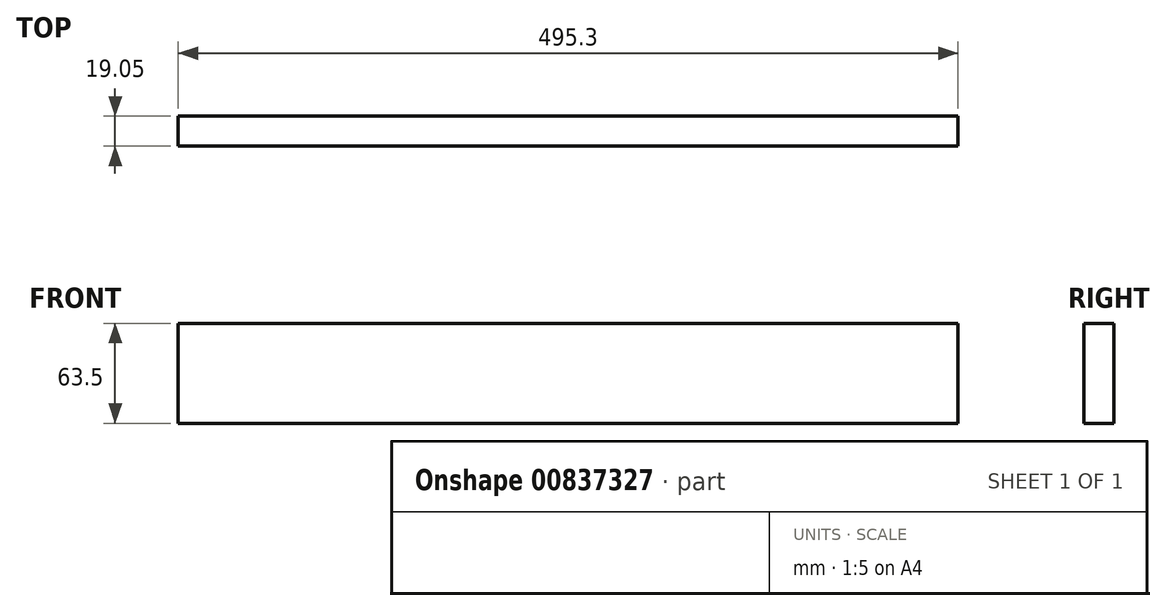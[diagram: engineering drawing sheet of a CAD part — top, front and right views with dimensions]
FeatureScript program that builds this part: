
annotation { "Feature Type Name" : "Feature", "Feature Type Description" : "" }
export const myFeature = defineFeature(function(context is Context, id is Id, definition is map)
    precondition{}
    {
        {
            var Q0;
            Q0=qCreatedBy(makeId("Front.planeOp"),FACE);
            var sketch = newSketch(context, id + "F0", { "sketchPlane" : qUnion([Q0])});
            skLineSegment(sketch, "E0.bottom", {"start": v(0, 0) * mm, "end": v(495.3, 0) * mm});
            skLineSegment(sketch, "E0.top", {"start": v(0, 63.5) * mm, "end": v(495.3, 63.5) * mm});
            skLineSegment(sketch, "E0.left", {"start": v(0, 0) * mm, "end": v(0, 63.5) * mm});
            skLineSegment(sketch, "E0.right", {"start": v(495.3, 0) * mm, "end": v(495.3, 63.5) * mm});
            skSolve(sketch);
        }
        {
            var Q0;
            Q0=makeQuery(id+"F0.imprint","IMPRINT",FACE,{"disambiguationData":[TD([[makeQuery(id+"F0.imprint","IMPRINT",EDGE,{"derivedFrom":sQuery(id+"F0.wireOp",EDGE,"E0.bottom")}),1.0]])]});
            extrude(context, id + "F1", {"entities" : qUnion([Q0]), "depth" : 19.05 * mm, "offsetDistance" : 25.4 * mm});
        }
    });
